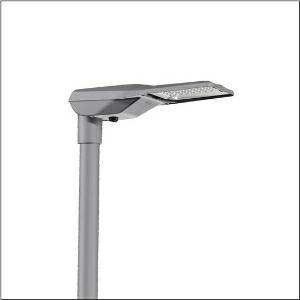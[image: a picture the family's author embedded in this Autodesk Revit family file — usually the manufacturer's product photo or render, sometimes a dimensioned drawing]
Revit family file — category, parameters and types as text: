
# Revit family: streetlight_sl_21_iq_mini___p0_5a_5xe2v31u08hb_fe50
name_source: partatom
category: Lighting Fixtures
units: mm (PartAtom-declared; Revit-internal decimal feet)

## family parameters
Cut with Voids When Loaded = No
Host = Face
Light Source = No
Part Type = Normal
Room Calculation Point = No
Round Connector Dimension = Use Diameter
Shared = No

## types (1)
- --- (1 x LED, 9580 lm, 71 W, 3000K)
    Apparent Load = 71 VA
    CIE Flux Codes = 37 73 96 100 100
    Color Rendering = 70
    Color Temperature = 3000K
    Default Elevation = 1800 mm
    Description = Streetlight SL 21 iQ mini, mast luminaire, primary light control with lens, of PMMA, primary optical cover: cover, of toughened safety glass, transparent, light distribution: P0.5a, light emission: direct distribution, primary light characteristic: asymmetric, installation type: post-top, side-entry, LED, High Power LED, rated luminous flux: 9.580lm, luminous efficacy: 135lm/W, light colour: 730, colour temperature: 3000K, control gear: iQ-Street Remote, D4i with power reduction, control: pre-setting: logarithmic dimming characteristic, Street-Remote, Auto-Match, Temp-Guard, Lumen-Switch, Night-Set, Smart-Wire, Light-Fading, Desk-Remote (wireless, voltage-free reading and setting of iQ features in the workshop via application-optimized NFC function/RFID function), optimised constant luminous flux control (CLO 2.0), mains connection: 220..240V, AC, 50/60Hz, start of lifetime: 71W, end of service life: 75W, reduction: 30W, luminaire housing, of diecast aluminium, powder-coated, Siteco® metallic grey (DB 702S), corrosivity category C5 mid according to DIN EN ISO 12944, please order mast flange separately, inclination adjustable: 0°, 5°, 10°, 15°, sealing non-destructively replaceable, multi-level sealing system, length: 628mm, width: 235mm, height: 110mm, mast flange for spigot size: 42mm (side-entry): 5XC10008XM4, 60/48mm (side-entry/post-top): 5XC10108XM2, 76/60mm (side-entry/post-top): 5XC10108XM1, mounting height: 4..8m, Smart Interface below, protection rating (complete): IP66, insulation class (complete): insulation class II (safety insulation), certification: CE, ENEC, ENEC+, VDE, impact resistance: IK10, permissible operating ambient temperature for outdoor applications: -40..+50°C, standard-compliant lighting for roads and squares, packaging unit: 1 piece

Light Distribution: P0.5a
    Height = 110 mm
    Lamp = 1 x LED
    Lamp Light Flux = 9580 lm
    Lamp Power = 71 W
    Lamp count = 1
    Length = 625 mm
    Luminous efficacy = 135 lm/W
    Manufacturer = Siteco
    ModVariant = No
    Model = 5XE2V31U08HB
    Number of Poles = 1
    OnlyDefault = Yes
    Power Factor = 1
    Product Name = Streetlight SL 21 iQ mini | P0.5a
    Product group = mast luminaire | pylon top
    ProductGroupID = 6100
    Protection Class = Protection class II
    Protection Degree = IP 66
    RLX_Detail_Level = 1
    RLX_Emergency_Light_Flux = 0 lm
    RLX_Emergency_Type = 0
    RLX_Emergency_Type_DB = No
    RlxData = <blob elided: 26057 chars, md5=8ffc9c1d>
    Socket = socket
    Standby Power = 0 W
    System Light Flux = 9580 lm
    System Power = 71 W
    Type Comments = factory setting: luminous flux: 100 % | dim-lin: 254 | 716 mA
    Type Image = l_1003516.jpg
    URL = http://relux.com
    VarID = @adj_070712
    Voltage = 0 V
    Weight = 0.00 kg
    Width = 234 mm

## geometry (parser evidence)
native form markers: Blend x4, Sweep x10
no freeform markers — native parametric forms only
